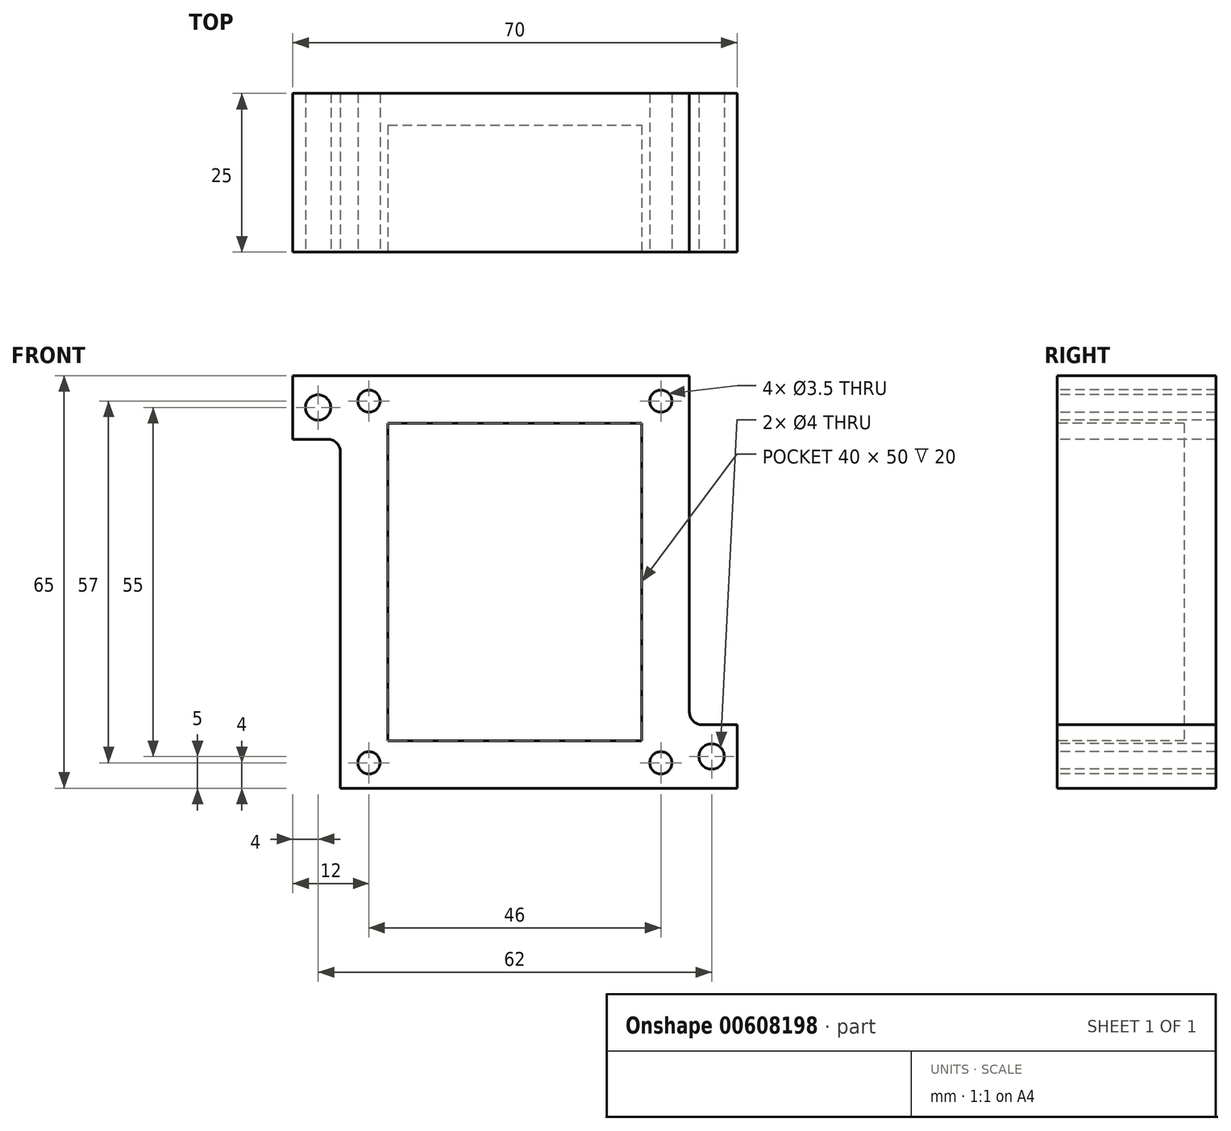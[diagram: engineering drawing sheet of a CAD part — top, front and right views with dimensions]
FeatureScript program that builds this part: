
annotation { "Feature Type Name" : "Feature", "Feature Type Description" : "" }
export const myFeature = defineFeature(function(context is Context, id is Id, definition is map)
    precondition{}
    {
        {
            var Q0;
            Q0=qCreatedBy(makeId("Front.planeOp"),FACE);
            var sketch = newSketch(context, id + "F0", { "sketchPlane" : qUnion([Q0])});
            skLineSegment(sketch, "E0.bottom", {"start": v(-35, 32.5) * mm, "end": v(35, 32.5) * mm});
            skLineSegment(sketch, "E0.top", {"start": v(-35, -32.5) * mm, "end": v(35, -32.5) * mm});
            skLineSegment(sketch, "E0.left", {"start": v(-35, 32.5) * mm, "end": v(-35, -32.5) * mm});
            skLineSegment(sketch, "E0.right", {"start": v(35, 32.5) * mm, "end": v(35, -32.5) * mm});
            skPoint(sketch, "E0.middle", {"position": v(0, 0) * mm});
            skSolve(sketch);
        }
        {
            var Q0;
            Q0=makeQuery(id+"F0.imprint","IMPRINT",FACE,{"disambiguationData":[TD([[makeQuery(id+"F0.imprint","IMPRINT",EDGE,{"derivedFrom":sQuery(id+"F0.wireOp",EDGE,"E0.bottom")}),-1.0]])]});
            extrude(context, id + "F1", {"entities" : qUnion([Q0]), "depth" : 25 * mm, "offsetDistance" : 25 * mm});
        }
        {
            var Q0;
            Q0=makeQuery(id+"F1.opExtrude","CAP_FACE",FACE,{"disambiguationData":[OSD([sQuery(id+"F0.wireOp",EDGE,"E0.bottom"),sQuery(id+"F0.wireOp",EDGE,"E0.top"),sQuery(id+"F0.wireOp",EDGE,"E0.left"),sQuery(id+"F0.wireOp",EDGE,"E0.right")])],"isStart":false});
            var sketch = newSketch(context, id + "F2", { "sketchPlane" : qUnion([Q0])});
            skLineSegment(sketch, "E1.bottom", {"start": v(-20, 25) * mm, "end": v(20, 25) * mm});
            skLineSegment(sketch, "E1.top", {"start": v(-20, -25) * mm, "end": v(20, -25) * mm});
            skLineSegment(sketch, "E1.left", {"start": v(-20, 25) * mm, "end": v(-20, -25) * mm});
            skLineSegment(sketch, "E1.right", {"start": v(20, 25) * mm, "end": v(20, -25) * mm});
            skPoint(sketch, "E1.middle", {"position": v(0, 0) * mm});
            skSolve(sketch);
        }
        {
            var Q0;
            Q0=makeQuery(id+"F2.imprint","IMPRINT",FACE,{"disambiguationData":[TD([[makeQuery(id+"F2.imprint","IMPRINT",EDGE,{"derivedFrom":sQuery(id+"F2.wireOp",EDGE,"E1.bottom")}),-1.0]])]});
            extrude(context, id + "F3", {"entities" : qUnion([Q0]), "operationType" : NewBodyOperationType.REMOVE, "oppositeDirection" : true, "depth" : 20 * mm, "offsetDistance" : 25 * mm});
        }
        {
            var Q0;
            Q0=makeQuery(id+"F1.opExtrude","CAP_FACE",FACE,{"disambiguationData":[OSD([sQuery(id+"F0.wireOp",EDGE,"E0.bottom"),sQuery(id+"F0.wireOp",EDGE,"E0.top"),sQuery(id+"F0.wireOp",EDGE,"E0.left"),sQuery(id+"F0.wireOp",EDGE,"E0.right")])],"isStart":false});
            var sketch = newSketch(context, id + "F4", { "sketchPlane" : qUnion([Q0])});
            skLineSegment(sketch, "E2.bottom", {"start": v(-35, -32.5) * mm, "end": v(-27.5, -32.5) * mm});
            skLineSegment(sketch, "E2.top", {"start": v(-35, 22.5) * mm, "end": v(-29.5, 22.5) * mm});
            skLineSegment(sketch, "E2.left", {"start": v(-35, -32.5) * mm, "end": v(-35, 22.5) * mm});
            skLineSegment(sketch, "E2.right", {"start": v(-27.5, -32.5) * mm, "end": v(-27.5, 20.5) * mm});
            skPoint(sketch, "E3.visualSharp", {"position": v(-27.5, 22.5) * mm});
            skArc(sketch, "E3.filletArc", {"start": v(-27.5, 20.5) * mm, "mid": v(-28.09, 21.91) * mm, "end": v(-29.5, 22.5) * mm});
            skSolve(sketch);
        }
        {
            var Q0;
            Q0 = qSketchRegion(id + "F4", true);
            extrude(context, id + "F5", {"entities" : qUnion([Q0]), "operationType" : NewBodyOperationType.REMOVE, "endBound" : BoundingType.THROUGH_ALL, "oppositeDirection" : true, "depth" : 25 * mm, "offsetDistance" : 25 * mm});
        }
        {
            var Q0;
            Q0=makeQuery(id+"F1.opExtrude","CAP_FACE",FACE,{"disambiguationData":[OSD([sQuery(id+"F0.wireOp",EDGE,"E0.bottom"),sQuery(id+"F0.wireOp",EDGE,"E0.top"),sQuery(id+"F0.wireOp",EDGE,"E0.left"),sQuery(id+"F0.wireOp",EDGE,"E0.right")])],"isStart":false});
            var sketch = newSketch(context, id + "F6", { "sketchPlane" : qUnion([Q0])});
            skLineSegment(sketch, "E4.bottom", {"start": v(35, 32.5) * mm, "end": v(27.5, 32.5) * mm});
            skLineSegment(sketch, "E4.top", {"start": v(35, -22.5) * mm, "end": v(29.5, -22.5) * mm});
            skLineSegment(sketch, "E4.left", {"start": v(35, 32.5) * mm, "end": v(35, -22.5) * mm});
            skLineSegment(sketch, "E4.right", {"start": v(27.5, 32.5) * mm, "end": v(27.5, -20.5) * mm});
            skPoint(sketch, "E5.visualSharp", {"position": v(27.5, -22.5) * mm});
            skArc(sketch, "E5.filletArc", {"start": v(27.5, -20.5) * mm, "mid": v(28.09, -21.91) * mm, "end": v(29.5, -22.5) * mm});
            skSolve(sketch);
        }
        {
            var Q0;
            Q0 = qSketchRegion(id + "F6", true);
            extrude(context, id + "F7", {"entities" : qUnion([Q0]), "operationType" : NewBodyOperationType.REMOVE, "endBound" : BoundingType.THROUGH_ALL, "oppositeDirection" : true, "depth" : 25 * mm, "offsetDistance" : 25 * mm});
        }
        {
            var Q0;
            Q0=makeQuery(id+"F1.opExtrude","CAP_FACE",FACE,{"disambiguationData":[OSD([sQuery(id+"F0.wireOp",EDGE,"E0.bottom"),sQuery(id+"F0.wireOp",EDGE,"E0.top"),sQuery(id+"F0.wireOp",EDGE,"E0.left"),sQuery(id+"F0.wireOp",EDGE,"E0.right")])],"isStart":false});
            var sketch = newSketch(context, id + "F8", { "sketchPlane" : qUnion([Q0])});
            skCircle(sketch, "E6", {"center": v(-31, 27.5) * mm, "radius": 2 * mm});
            skCircle(sketch, "E7", {"center": v(31, -27.5) * mm, "radius": 2 * mm});
            skPoint(sketch, "E8", {"position": v(-35, 27.5) * mm});
            skPoint(sketch, "E9", {"position": v(35, -27.5) * mm});
            skCircle(sketch, "E10", {"center": v(-23, 28.5) * mm, "radius": 1.75 * mm});
            skCircle(sketch, "E11", {"center": v(23, 28.5) * mm, "radius": 1.75 * mm});
            skCircle(sketch, "E12.MirrorC", {"center": v(-23, -28.5) * mm, "radius": 1.75 * mm});
            skCircle(sketch, "E13.MirrorC", {"center": v(23, -28.5) * mm, "radius": 1.75 * mm});
            skSolve(sketch);
        }
        {
            var Q0;
            Q0 = qSketchRegion(id + "F8", true);
            extrude(context, id + "F9", {"entities" : qUnion([Q0]), "operationType" : NewBodyOperationType.REMOVE, "endBound" : BoundingType.THROUGH_ALL, "oppositeDirection" : true, "depth" : 25 * mm, "offsetDistance" : 25 * mm});
        }
    });
